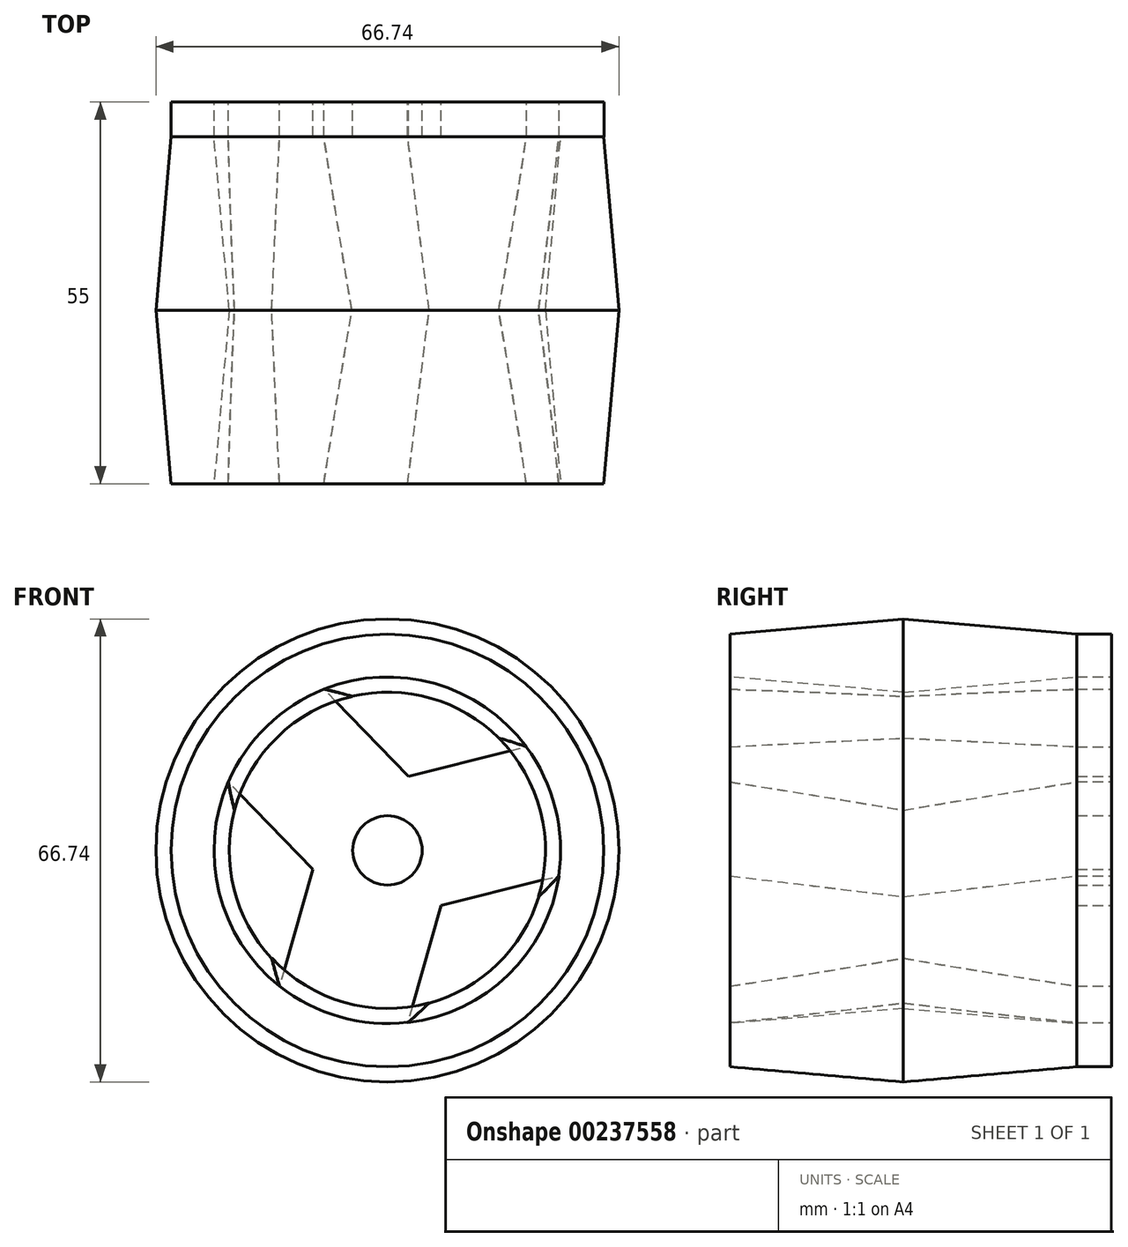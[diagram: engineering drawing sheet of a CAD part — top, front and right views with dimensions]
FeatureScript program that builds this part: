
annotation { "Feature Type Name" : "Feature", "Feature Type Description" : "" }
export const myFeature = defineFeature(function(context is Context, id is Id, definition is map)
    precondition{}
    {
        {
            var Q0;
            Q0=qCreatedBy(makeId("Front.planeOp"),FACE);
            var sketch = newSketch(context, id + "F0", { "sketchPlane" : qUnion([Q0])});
            skArc(sketch, "E0", {"start": v(-19.65, 52.13) * mm, "mid": v(-57.1, 55.14) * mm, "end": v(-55.25, 17.62) * mm});
            skCircle(sketch, "E1", {"center": v(-39.7, 37.2) * mm, "radius": 31.2 * mm});
            skPoint(sketch, "E2.0.midPoint", {"position": v(-31.26, 28.49) * mm});
            skPoint(sketch, "E3.0.midPoint", {"position": v(-43.56, 41.17) * mm});
            skLineSegment(sketch, "E4", {"start": v(-31.98, 29.23) * mm, "end": v(-36.77, 12.36) * mm});
            skLineSegment(sketch, "E5", {"start": v(-50.45, 34.49) * mm, "end": v(-55.25, 17.62) * mm});
            skLineSegment(sketch, "E6", {"start": v(-36.66, 47.86) * mm, "end": v(-19.65, 52.13) * mm});
            skLineSegment(sketch, "E7", {"start": v(-31.98, 29.23) * mm, "end": v(-14.97, 33.5) * mm});
            skLineSegment(sketch, "E8", {"start": v(-36.66, 47.86) * mm, "end": v(-48.87, 60.45) * mm});
            skLineSegment(sketch, "E9", {"start": v(-50.45, 34.49) * mm, "end": v(-62.66, 47.07) * mm});
            skPoint(sketch, "E10.orphan", {"position": v(-16.18, 43.1) * mm});
            skPoint(sketch, "E11.orphan", {"position": v(-46.33, 13.87) * mm});
            skArc(sketch, "E12.trimOffspring", {"start": v(-36.77, 12.36) * mm, "mid": v(-22.3, 19.24) * mm, "end": v(-14.97, 33.5) * mm});
            skCircle(sketch, "E13", {"center": v(-39.7, 37.2) * mm, "radius": 5 * mm});
            skSolve(sketch);
        }
        {
            var Q0;
            Q0=makeQuery(id+"F0.imprint","IMPRINT",FACE,{"disambiguationData":[TD([[makeQuery(id+"F0.imprint","IMPRINT",EDGE,{"derivedFrom":sQuery(id+"F0.wireOp",EDGE,"E1")}),1.0]])]});
            extrude(context, id + "F1", {"entities" : qUnion([Q0]), "depth" : 5 * mm});
        }
        {
            var Q0;
            Q0=makeQuery(id+"F1.opExtrude","CAP_FACE",FACE,{"disambiguationData":[OSD([sQuery(id+"F0.wireOp",EDGE,"E0"),sQuery(id+"F0.wireOp",EDGE,"E1"),sQuery(id+"F0.wireOp",EDGE,"E4"),sQuery(id+"F0.wireOp",EDGE,"E5"),sQuery(id+"F0.wireOp",EDGE,"E6"),sQuery(id+"F0.wireOp",EDGE,"E7"),sQuery(id+"F0.wireOp",EDGE,"E8"),sQuery(id+"F0.wireOp",EDGE,"E9"),sQuery(id+"F0.wireOp",EDGE,"E12.trimOffspring")])],"isStart":false});
            var sketch = newSketch(context, id + "F2", { "sketchPlane" : qUnion([Q0])});
            skCircle(sketch, "E14", {"center": v(-39.7, 37.2) * mm, "radius": 31.18 * mm});
            skCircle(sketch, "E15", {"center": v(-39.7, 37.2) * mm, "radius": 24.96 * mm});
            skSolve(sketch);
        }
        {
            var Q0;
            Q0=makeQuery(id+"F2.imprint","IMPRINT",FACE,{"disambiguationData":[TD([[makeQuery(id+"F2.imprint","IMPRINT",EDGE,{"derivedFrom":sQuery(id+"F2.wireOp",EDGE,"E14")}),1.0]])]});
            extrude(context, id + "F3", {"entities" : qUnion([Q0]), "operationType" : NewBodyOperationType.ADD, "depth" : 25 * mm, "hasDraft" : true, "draftAngle" : 5 * degree});
        }
        {
            var Q0;
            Q0=makeQuery(id+"F3.opExtrude","CAP_FACE",FACE,{"disambiguationData":[OSD([sQuery(id+"F0.wireOp",EDGE,"E0"),sQuery(id+"F0.wireOp",EDGE,"E4"),sQuery(id+"F0.wireOp",EDGE,"E5"),sQuery(id+"F0.wireOp",EDGE,"E6"),sQuery(id+"F0.wireOp",EDGE,"E7"),sQuery(id+"F0.wireOp",EDGE,"E8"),sQuery(id+"F0.wireOp",EDGE,"E9"),sQuery(id+"F0.wireOp",EDGE,"E12.trimOffspring"),sQuery(id+"F2.wireOp",EDGE,"E14"),sQuery(id+"F2.wireOp",EDGE,"E15")])],"isStart":false});
            extrude(context, id + "F4", {"entities" : qUnion([Q0]), "operationType" : NewBodyOperationType.ADD, "depth" : 25 * mm, "hasDraft" : true, "draftAngle" : 5 * degree, "draftPullDirection" : true});
        }
    });
